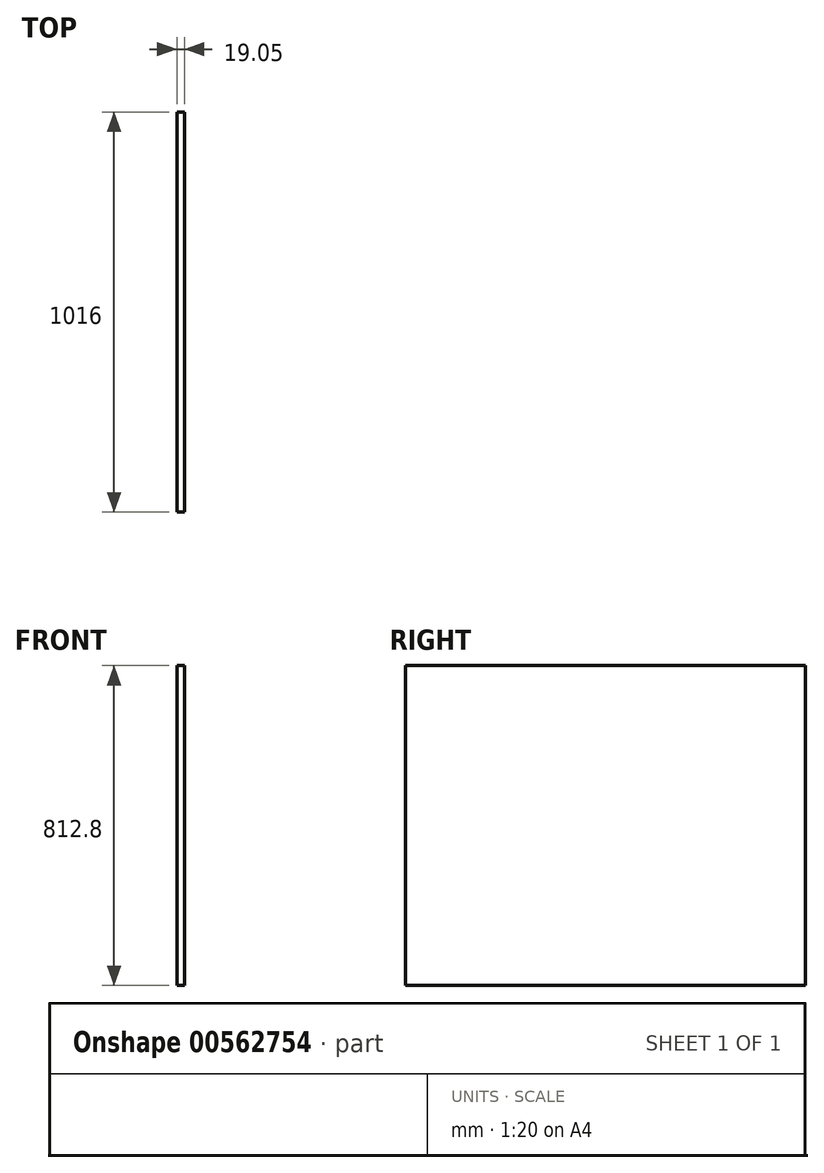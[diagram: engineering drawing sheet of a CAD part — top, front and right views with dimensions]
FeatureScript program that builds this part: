
annotation { "Feature Type Name" : "Feature", "Feature Type Description" : "" }
export const myFeature = defineFeature(function(context is Context, id is Id, definition is map)
    precondition{}
    {
        {
            var Q0;
            Q0=qCreatedBy(makeId("Right.planeOp"),FACE);
            var sketch = newSketch(context, id + "F0", { "sketchPlane" : qUnion([Q0])});
            skLineSegment(sketch, "E0.bottom", {"start": v(-508, -406.4) * mm, "end": v(508, -406.4) * mm});
            skLineSegment(sketch, "E0.top", {"start": v(-508, 406.4) * mm, "end": v(508, 406.4) * mm});
            skLineSegment(sketch, "E0.left", {"start": v(-508, -406.4) * mm, "end": v(-508, 406.4) * mm});
            skLineSegment(sketch, "E0.right", {"start": v(508, -406.4) * mm, "end": v(508, 406.4) * mm});
            skPoint(sketch, "E0.middle", {"position": v(0, 0) * mm});
            skSolve(sketch);
        }
        {
            var Q0;
            Q0 = qSketchRegion(id + "F0", true);
            extrude(context, id + "F1", {"entities" : qUnion([Q0]), "depth" : 19.05 * mm, "offsetDistance" : 25.4 * mm});
        }
    });
